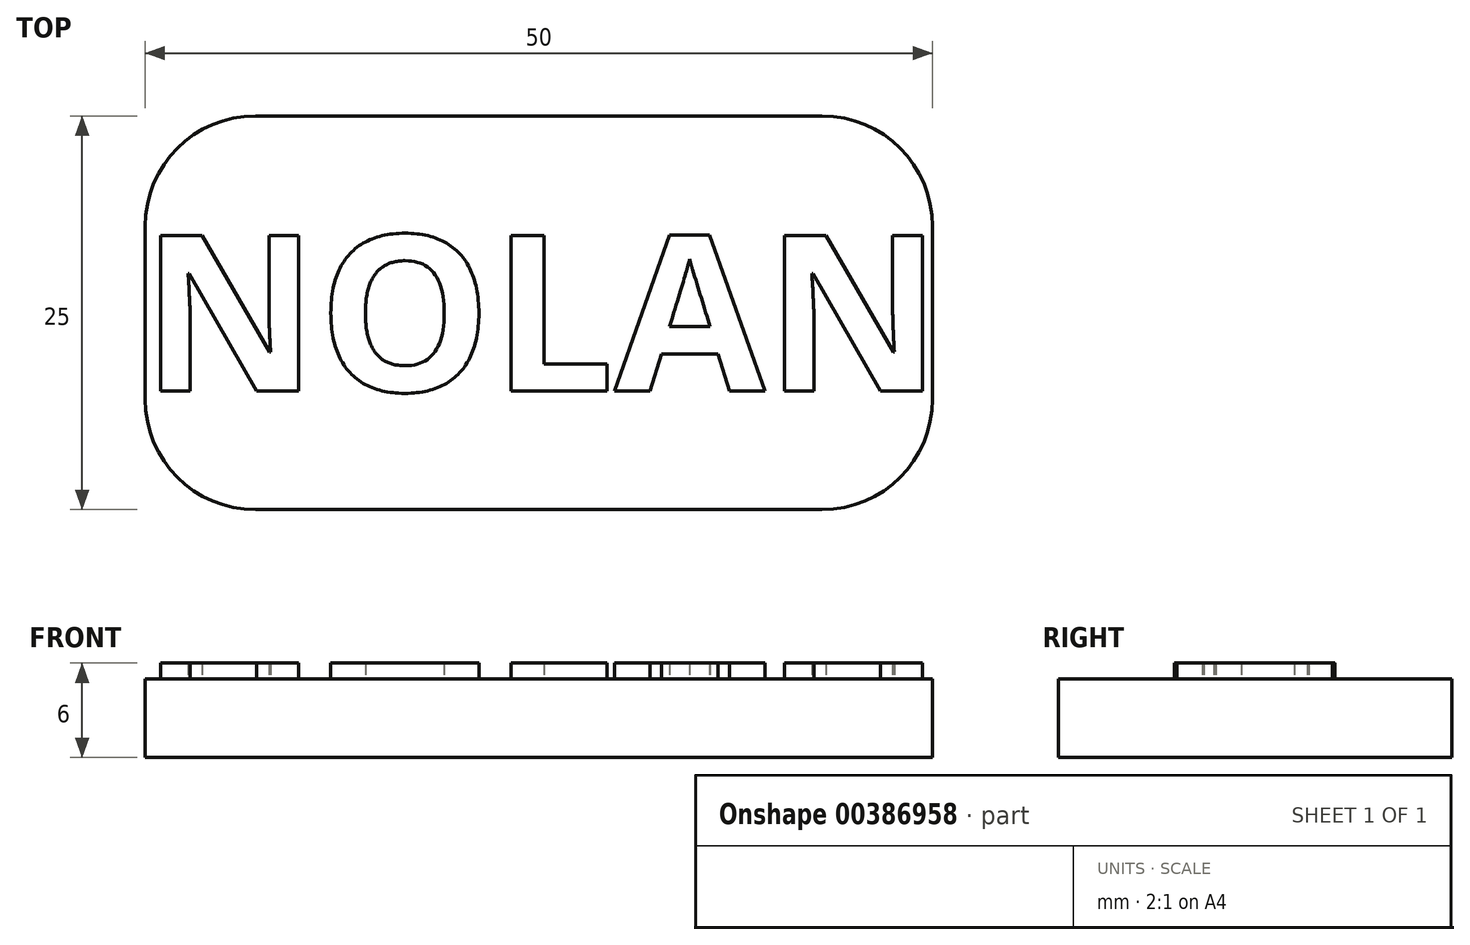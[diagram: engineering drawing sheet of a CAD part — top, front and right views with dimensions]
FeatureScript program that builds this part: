
annotation { "Feature Type Name" : "Feature", "Feature Type Description" : "" }
export const myFeature = defineFeature(function(context is Context, id is Id, definition is map)
    precondition{}
    {
        {
            var Q0;
            Q0=qCreatedBy(makeId("Top.planeOp"),FACE);
            var sketch = newSketch(context, id + "F0", { "sketchPlane" : qUnion([Q0])});
            skLineSegment(sketch, "E0.bottom", {"start": v(0, 0) * mm, "end": v(50, 0) * mm});
            skLineSegment(sketch, "E0.top", {"start": v(0, 25) * mm, "end": v(50, 25) * mm});
            skLineSegment(sketch, "E0.left", {"start": v(0, 0) * mm, "end": v(0, 25) * mm});
            skLineSegment(sketch, "E0.right", {"start": v(50, 0) * mm, "end": v(50, 25) * mm});
            skSolve(sketch);
        }
        {
            var Q0;
            Q0 = qSketchRegion(id + "F0", true);
            extrude(context, id + "F1", {"entities" : qUnion([Q0]), "depth" : 5 * mm});
        }
        {
            var Q0;
            Q0=makeQuery(id+"F1.opExtrude","CAP_FACE",FACE,{"disambiguationData":[OSD([sQuery(id+"F0.wireOp",EDGE,"E0.bottom"),sQuery(id+"F0.wireOp",EDGE,"E0.top"),sQuery(id+"F0.wireOp",EDGE,"E0.left"),sQuery(id+"F0.wireOp",EDGE,"E0.right")])],"isStart":false});
            var sketch = newSketch(context, id + "F2", { "sketchPlane" : qUnion([Q0])});
            skText(sketch, "E1", { "text": "NOLAN", "fontName": "OpenSans-Bold.ttf"});
            skPoint(sketch, "E1.secondSnap0", {"position": v(-0.95, 17.48) * mm});
            skLineSegment(sketch, "E2", {"start": v(-6.58, 12.5) * mm, "end": v(52.99, 12.5) * mm, "construction": true});
            skLineSegment(sketch, "E3", {"start": v(25, 25) * mm, "end": v(25, 0) * mm, "construction": true});
            const initialGuessF2  = {"E1": [-0.00026, 0.00752, 1, 0, 0.00996]};
            skSetInitialGuess(sketch, initialGuessF2);
            skSolve(sketch);
        }
        {
            var Q0;
            Q0 = qSketchRegion(id + "F2", true);
            extrude(context, id + "F3", {"entities" : qUnion([Q0]), "operationType" : NewBodyOperationType.ADD, "depth" : 1 * mm});
        }
        {
            var Q0;
            Q0=makeQuery(id+"F1.opExtrude","SWEPT_EDGE",EDGE,{"disambiguationData":[OSD([sQuery(id+"F0.wireOp",EDGE,"E0.top"),sQuery(id+"F0.wireOp",EDGE,"E0.left")])]});
            var Q1;
            Q1=makeQuery(id+"F1.opExtrude","SWEPT_EDGE",EDGE,{"disambiguationData":[OSD([sQuery(id+"F0.wireOp",EDGE,"E0.bottom"),sQuery(id+"F0.wireOp",EDGE,"E0.left")])]});
            var Q2;
            Q2=makeQuery(id+"F1.opExtrude","SWEPT_EDGE",EDGE,{"disambiguationData":[OSD([sQuery(id+"F0.wireOp",EDGE,"E0.top"),sQuery(id+"F0.wireOp",EDGE,"E0.right")])]});
            var Q3;
            Q3=makeQuery(id+"F1.opExtrude","SWEPT_EDGE",EDGE,{"disambiguationData":[OSD([sQuery(id+"F0.wireOp",EDGE,"E0.bottom"),sQuery(id+"F0.wireOp",EDGE,"E0.right")])]});
            fillet(context, id + "F4", {"entities" : qUnion([Q0, Q1, Q2, Q3]), "radius" : 7 * mm, "tangentPropagation" : true, "allowEdgeOverflow" : false});
        }
    });
